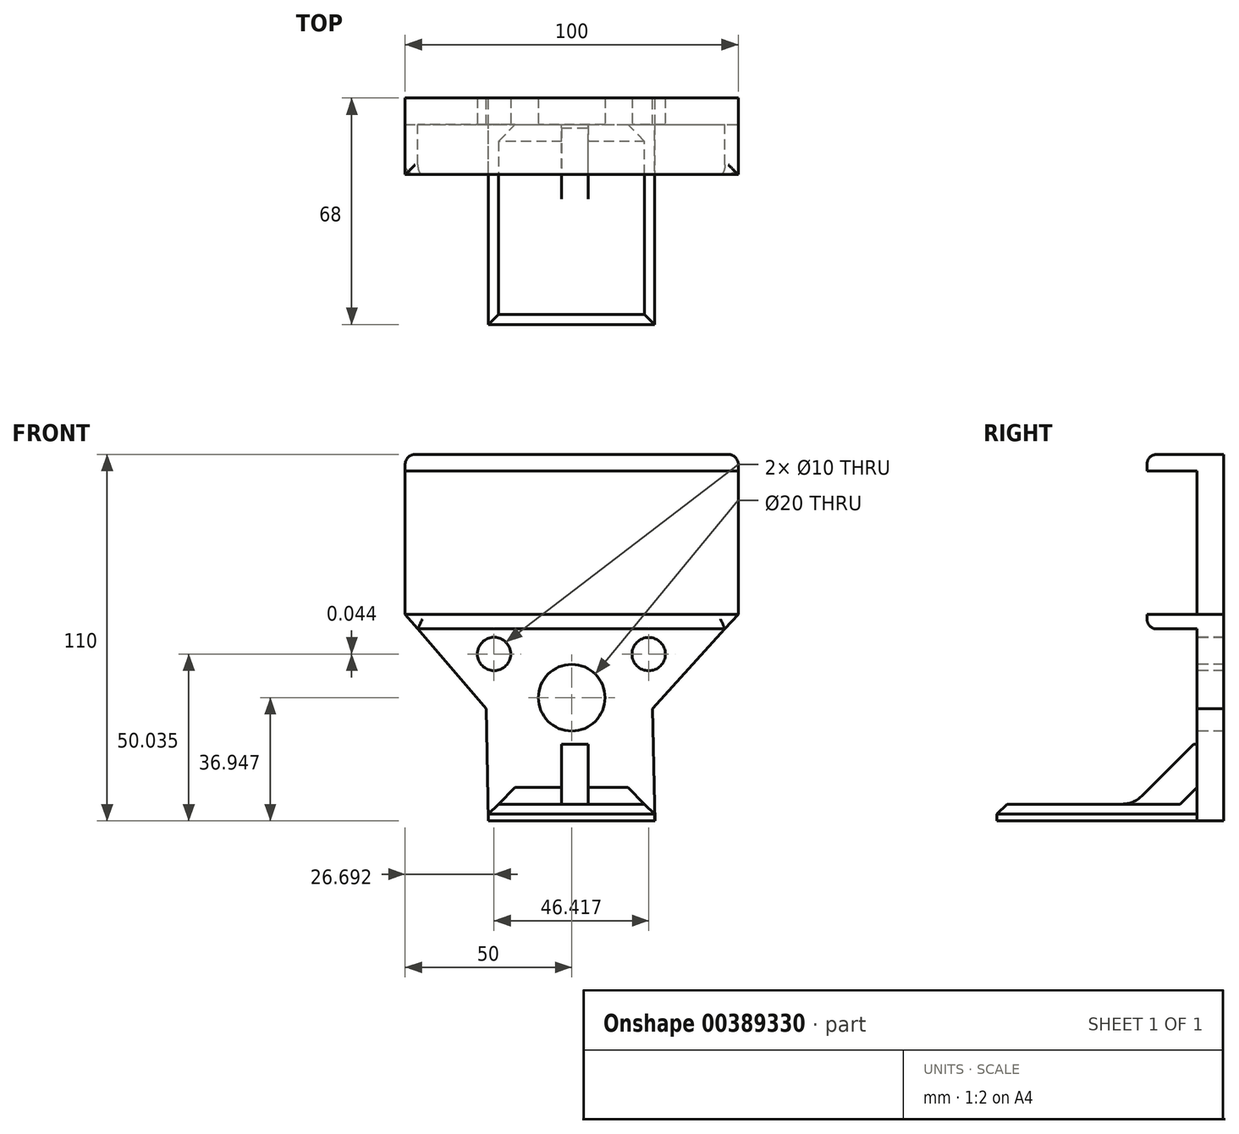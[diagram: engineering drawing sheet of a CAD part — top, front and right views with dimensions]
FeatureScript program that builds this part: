
annotation { "Feature Type Name" : "Feature", "Feature Type Description" : "" }
export const myFeature = defineFeature(function(context is Context, id is Id, definition is map)
    precondition{}
    {
        {
            var Q0;
            Q0=qCreatedBy(makeId("Front.planeOp"),FACE);
            var sketch = newSketch(context, id + "F0", { "sketchPlane" : qUnion([Q0])});
            skLineSegment(sketch, "E0", {"start": v(-25.7, 33.67) * mm, "end": v(-25, 0) * mm});
            skLineSegment(sketch, "E1", {"start": v(-25, 0) * mm, "end": v(0, 0) * mm});
            skLineSegment(sketch, "E2", {"start": v(24.3, 33.67) * mm, "end": v(25, 0) * mm});
            skLineSegment(sketch, "E3", {"start": v(25, 0) * mm, "end": v(0, 0) * mm});
            skLineSegment(sketch, "E4", {"start": v(-25.7, 33.67) * mm, "end": v(-50, 62) * mm});
            skLineSegment(sketch, "E5", {"start": v(24.3, 33.67) * mm, "end": v(50, 62) * mm});
            skLineSegment(sketch, "E6", {"start": v(-50, 62) * mm, "end": v(50, 62) * mm});
            skLineSegment(sketch, "E7", {"start": v(0, 62) * mm, "end": v(0, 0) * mm});
            skSolve(sketch);
        }
        {
            var Q0;
            Q0 = qSketchRegion(id + "F0", true);
            extrude(context, id + "F1", {"entities" : qUnion([Q0]), "depth" : 8 * mm, "offsetDistance" : 25 * mm});
        }
        {
            var Q0;
            Q0=makeQuery(id+"F1.opExtrude","CAP_FACE",FACE,{"disambiguationData":[OSD([sQuery(id+"F0.wireOp",EDGE,"E0"),sQuery(id+"F0.wireOp",EDGE,"E1"),sQuery(id+"F0.wireOp",EDGE,"E2"),sQuery(id+"F0.wireOp",EDGE,"E3"),sQuery(id+"F0.wireOp",EDGE,"E4"),sQuery(id+"F0.wireOp",EDGE,"E5"),sQuery(id+"F0.wireOp",EDGE,"E6")])],"isStart":false});
            var sketch = newSketch(context, id + "F2", { "sketchPlane" : qUnion([Q0])});
            skLineSegment(sketch, "E8.bottom", {"start": v(-25, 0) * mm, "end": v(24.9, 0) * mm});
            skLineSegment(sketch, "E8.top", {"start": v(-25, 5) * mm, "end": v(24.9, 5) * mm});
            skLineSegment(sketch, "E8.left", {"start": v(-25, 0) * mm, "end": v(-25, 5) * mm});
            skLineSegment(sketch, "E8.right", {"start": v(24.9, 0) * mm, "end": v(24.9, 5) * mm});
            skSolve(sketch);
        }
        {
            var Q0;
            Q0=makeQuery(id+"F2.imprint","IMPRINT",FACE,{"disambiguationData":[TD([[makeQuery(id+"F2.imprint","IMPRINT",EDGE,{"derivedFrom":sQuery(id+"F2.wireOp",EDGE,"E8.bottom")}),1.0]])]});
            extrude(context, id + "F3", {"entities" : qUnion([Q0]), "operationType" : NewBodyOperationType.ADD, "depth" : 60 * mm, "offsetDistance" : 25 * mm});
        }
        {
            var Q0;
            {var subQ0=sQuery(id+"F0.wireOp",EDGE,"E2");var subQ1=sQuery(id+"F0.wireOp",EDGE,"E6");var subQ2=sQuery(id+"F0.wireOp",EDGE,"E5");var subQ3=sQuery(id+"F0.wireOp",EDGE,"E4");var subQ4=sQuery(id+"F0.wireOp",EDGE,"E0");var subQ5=sQuery(id+"F0.wireOp",EDGE,"E3");var subQ6=sQuery(id+"F0.wireOp",EDGE,"E1");var subQ7=makeQuery(id+"F1.opExtrude","CAP_FACE",FACE,{"disambiguationData":[OSD([subQ4,subQ6,subQ0,subQ5,subQ3,subQ2,subQ1])],"isStart":false});Q0=makeQuery(id+"F3.boolean.opBoolean","SPLIT",FACE,{"disambiguationData":[TD([makeQuery(id+"F1.opExtrude","SWEPT_FACE",FACE,{"disambiguationData":[OSD([subQ4])]}),subQ7,makeQuery(id+"F1.opExtrude","SWEPT_FACE",FACE,{"disambiguationData":[OSD([subQ6,subQ5])]}),makeQuery(id+"F1.opExtrude","SWEPT_FACE",FACE,{"disambiguationData":[OSD([subQ0])]}),makeQuery(id+"F1.opExtrude","SWEPT_FACE",FACE,{"disambiguationData":[OSD([subQ3])]}),makeQuery(id+"F1.opExtrude","SWEPT_FACE",FACE,{"disambiguationData":[OSD([subQ2])]}),makeQuery(id+"F1.opExtrude","SWEPT_FACE",FACE,{"disambiguationData":[OSD([subQ1])]}),makeQuery(id+"F3.opExtrude","SWEPT_FACE",FACE,{"disambiguationData":[OSD([sQuery(id+"F2.wireOp",EDGE,"E8.bottom")])]}),makeQuery(id+"F3.opExtrude","SWEPT_FACE",FACE,{"disambiguationData":[OSD([sQuery(id+"F2.wireOp",EDGE,"E8.top")])]}),makeQuery(id+"F3.opExtrude","SWEPT_FACE",FACE,{"disambiguationData":[OSD([sQuery(id+"F2.wireOp",EDGE,"E8.left")])]}),makeQuery(id+"F3.opExtrude","SWEPT_FACE",FACE,{"disambiguationData":[OSD([sQuery(id+"F2.wireOp",EDGE,"E8.right")])]})])],"derivedFrom":subQ7});}
            var sketch = newSketch(context, id + "F4", { "sketchPlane" : qUnion([Q0])});
            skLineSegment(sketch, "E9.bottom", {"start": v(-3.01, 5) * mm, "end": v(4.99, 5) * mm});
            skLineSegment(sketch, "E9.top", {"start": v(-3.01, 23) * mm, "end": v(4.99, 23) * mm});
            skLineSegment(sketch, "E9.left", {"start": v(-3.01, 5) * mm, "end": v(-3.01, 23) * mm});
            skLineSegment(sketch, "E9.right", {"start": v(4.99, 5) * mm, "end": v(4.99, 23) * mm});
            skSolve(sketch);
        }
        {
            var Q0;
            Q0 = qSketchRegion(id + "F4", true);
            extrude(context, id + "F5", {"entities" : qUnion([Q0]), "operationType" : NewBodyOperationType.ADD, "depth" : 20 * mm, "offsetDistance" : 25 * mm});
        }
        {
            var Q0;
            Q0=makeQuery(id+"F5.opExtrude","CAP_EDGE",EDGE,{"disambiguationData":[OSD([sQuery(id+"F4.wireOp",EDGE,"E9.top")])],"isStart":false});
            chamfer(context, id + "F6", {"entities" : qUnion([Q0]), "width" : 19 * mm, "tangentPropagation" : true});
        }
        {
            var Q0;
            Q0=makeQuery(id+"F3.opExtrude","SWEPT_EDGE",EDGE,{"disambiguationData":[OSD([sQuery(id+"F2.wireOp",EDGE,"E8.top"),sQuery(id+"F2.wireOp",EDGE,"E8.left")])]});
            var Q1;
            Q1=makeQuery(id+"F3.opExtrude","CAP_EDGE",EDGE,{"disambiguationData":[OSD([sQuery(id+"F2.wireOp",EDGE,"E8.top")])],"isStart":false});
            var Q2;
            Q2=makeQuery(id+"F3.opExtrude","SWEPT_EDGE",EDGE,{"disambiguationData":[OSD([sQuery(id+"F0.wireOp",EDGE,"E2"),sQuery(id+"F2.wireOp",EDGE,"E8.top"),sQuery(id+"F2.wireOp",EDGE,"E8.right")])]});
            chamfer(context, id + "F7", {"entities" : qUnion([Q0, Q1, Q2]), "width" : 3 * mm, "tangentPropagation" : true});
        }
        {
            var Q0;
            {var subQ0=makeQuery(id+"F3.opExtrude","SWEPT_FACE",FACE,{"disambiguationData":[OSD([sQuery(id+"F2.wireOp",EDGE,"E8.bottom")])]});var subQ1=sQuery(id+"F0.wireOp",EDGE,"E2");var subQ2=makeQuery(id+"F1.opExtrude","SWEPT_FACE",FACE,{"disambiguationData":[OSD([subQ1])]});var subQ3=sQuery(id+"F0.wireOp",EDGE,"E6");var subQ4=makeQuery(id+"F3.opExtrude","SWEPT_FACE",FACE,{"disambiguationData":[OSD([sQuery(id+"F2.wireOp",EDGE,"E8.top")])]});var subQ5=sQuery(id+"F0.wireOp",EDGE,"E5");var subQ6=sQuery(id+"F0.wireOp",EDGE,"E4");var subQ7=sQuery(id+"F0.wireOp",EDGE,"E0");var subQ8=sQuery(id+"F0.wireOp",EDGE,"E3");var subQ9=sQuery(id+"F0.wireOp",EDGE,"E1");var subQ10=makeQuery(id+"F1.opExtrude","CAP_FACE",FACE,{"disambiguationData":[OSD([subQ7,subQ9,subQ1,subQ8,subQ6,subQ5,subQ3])],"isStart":false});var subQ11=makeQuery(id+"F1.opExtrude","SWEPT_FACE",FACE,{"disambiguationData":[OSD([subQ9,subQ8])]});var subQ12=makeQuery(id+"F3.opExtrude","SWEPT_FACE",FACE,{"disambiguationData":[OSD([sQuery(id+"F2.wireOp",EDGE,"E8.right")])]});Q0=makeQuery(id+"F7.opChamfer","MERGE",FACE,{"derivedFrom":[makeQuery(id+"F3.boolean.opBoolean","SPLIT",FACE,{"disambiguationData":[TD([subQ10,subQ11,subQ2,subQ0,subQ4,subQ12])],"derivedFrom":subQ10}),makeQuery(id+"F3.boolean.opBoolean","SPLIT",FACE,{"disambiguationData":[TD([makeQuery(id+"F1.opExtrude","SWEPT_FACE",FACE,{"disambiguationData":[OSD([subQ7])]}),subQ10,subQ11,subQ2,makeQuery(id+"F1.opExtrude","SWEPT_FACE",FACE,{"disambiguationData":[OSD([subQ6])]}),makeQuery(id+"F1.opExtrude","SWEPT_FACE",FACE,{"disambiguationData":[OSD([subQ5])]}),makeQuery(id+"F1.opExtrude","SWEPT_FACE",FACE,{"disambiguationData":[OSD([subQ3])]}),subQ0,subQ4,makeQuery(id+"F3.opExtrude","SWEPT_FACE",FACE,{"disambiguationData":[OSD([sQuery(id+"F2.wireOp",EDGE,"E8.left")])]}),subQ12])],"derivedFrom":subQ10})]});}
            var sketch = newSketch(context, id + "F8", { "sketchPlane" : qUnion([Q0])});
            skCircle(sketch, "E10", {"center": v(0, 36.95) * mm, "radius": 10 * mm});
            skCircle(sketch, "E11", {"center": v(-23.3, 50.08) * mm, "radius": 5 * mm});
            skCircle(sketch, "E12", {"center": v(23.1, 50.03) * mm, "radius": 5 * mm});
            skSolve(sketch);
        }
        {
            var Q0;
            Q0=makeQuery(id+"F8.imprint","IMPRINT",FACE,{"disambiguationData":[TD([[makeQuery(id+"F8.imprint","IMPRINT",EDGE,{"derivedFrom":sQuery(id+"F8.wireOp",EDGE,"E11")}),1.0]])]});
            var Q1;
            Q1=makeQuery(id+"F8.imprint","IMPRINT",FACE,{"disambiguationData":[TD([[makeQuery(id+"F8.imprint","IMPRINT",EDGE,{"derivedFrom":sQuery(id+"F8.wireOp",EDGE,"E10")}),1.0]])]});
            var Q2;
            Q2=makeQuery(id+"F8.imprint","IMPRINT",FACE,{"disambiguationData":[TD([[makeQuery(id+"F8.imprint","IMPRINT",EDGE,{"derivedFrom":sQuery(id+"F8.wireOp",EDGE,"E12")}),1.0]])]});
            var Q3;
            Q3=sQuery(id+"F8.wireOp",EDGE,"E11");
            var Q4;
            Q4=sQuery(id+"F8.wireOp",EDGE,"E10");
            var Q5;
            Q5=sQuery(id+"F8.wireOp",EDGE,"E12");
            extrude(context, id + "F9", {"entities" : qUnion([Q0, Q1, Q2]), "operationType" : NewBodyOperationType.REMOVE, "surfaceEntities" : qUnion([Q3, Q4, Q5]), "oppositeDirection" : true, "depth" : 25 * mm, "offsetDistance" : 25 * mm});
        }
        {
            var Q0;
            {var subQ0=sQuery(id+"F0.wireOp",EDGE,"E2");var subQ1=sQuery(id+"F0.wireOp",EDGE,"E6");var subQ2=sQuery(id+"F0.wireOp",EDGE,"E5");var subQ3=sQuery(id+"F0.wireOp",EDGE,"E4");var subQ4=sQuery(id+"F0.wireOp",EDGE,"E0");var subQ5=sQuery(id+"F0.wireOp",EDGE,"E3");var subQ6=sQuery(id+"F0.wireOp",EDGE,"E1");var subQ7=makeQuery(id+"F1.opExtrude","CAP_FACE",FACE,{"disambiguationData":[OSD([subQ4,subQ6,subQ0,subQ5,subQ3,subQ2,subQ1])],"isStart":false});Q0=makeQuery(id+"F6.opChamfer","BLEND_EDGE",EDGE,{"blendedFrom":[makeQuery(id+"F5.opExtrude","CAP_EDGE",EDGE,{"disambiguationData":[OSD([sQuery(id+"F4.wireOp",EDGE,"E9.top")])],"isStart":false}),makeQuery(id+"F3.boolean.opBoolean","SPLIT",FACE,{"disambiguationData":[TD([makeQuery(id+"F1.opExtrude","SWEPT_FACE",FACE,{"disambiguationData":[OSD([subQ4])]}),subQ7,makeQuery(id+"F1.opExtrude","SWEPT_FACE",FACE,{"disambiguationData":[OSD([subQ6,subQ5])]}),makeQuery(id+"F1.opExtrude","SWEPT_FACE",FACE,{"disambiguationData":[OSD([subQ0])]}),makeQuery(id+"F1.opExtrude","SWEPT_FACE",FACE,{"disambiguationData":[OSD([subQ3])]}),makeQuery(id+"F1.opExtrude","SWEPT_FACE",FACE,{"disambiguationData":[OSD([subQ2])]}),makeQuery(id+"F1.opExtrude","SWEPT_FACE",FACE,{"disambiguationData":[OSD([subQ1])]}),makeQuery(id+"F3.opExtrude","SWEPT_FACE",FACE,{"disambiguationData":[OSD([sQuery(id+"F2.wireOp",EDGE,"E8.bottom")])]}),makeQuery(id+"F3.opExtrude","SWEPT_FACE",FACE,{"disambiguationData":[OSD([sQuery(id+"F2.wireOp",EDGE,"E8.top")])]}),makeQuery(id+"F3.opExtrude","SWEPT_FACE",FACE,{"disambiguationData":[OSD([sQuery(id+"F2.wireOp",EDGE,"E8.left")])]}),makeQuery(id+"F3.opExtrude","SWEPT_FACE",FACE,{"disambiguationData":[OSD([sQuery(id+"F2.wireOp",EDGE,"E8.right")])]})])],"derivedFrom":subQ7})],"blendedInto":[makeQuery(id+"F3.boolean.opBoolean","SPLIT",FACE,{"disambiguationData":[TD([makeQuery(id+"F1.opExtrude","SWEPT_FACE",FACE,{"disambiguationData":[OSD([subQ4])]}),subQ7,makeQuery(id+"F1.opExtrude","SWEPT_FACE",FACE,{"disambiguationData":[OSD([subQ6,subQ5])]}),makeQuery(id+"F1.opExtrude","SWEPT_FACE",FACE,{"disambiguationData":[OSD([subQ0])]}),makeQuery(id+"F1.opExtrude","SWEPT_FACE",FACE,{"disambiguationData":[OSD([subQ3])]}),makeQuery(id+"F1.opExtrude","SWEPT_FACE",FACE,{"disambiguationData":[OSD([subQ2])]}),makeQuery(id+"F1.opExtrude","SWEPT_FACE",FACE,{"disambiguationData":[OSD([subQ1])]}),makeQuery(id+"F3.opExtrude","SWEPT_FACE",FACE,{"disambiguationData":[OSD([sQuery(id+"F2.wireOp",EDGE,"E8.bottom")])]}),makeQuery(id+"F3.opExtrude","SWEPT_FACE",FACE,{"disambiguationData":[OSD([sQuery(id+"F2.wireOp",EDGE,"E8.top")])]}),makeQuery(id+"F3.opExtrude","SWEPT_FACE",FACE,{"disambiguationData":[OSD([sQuery(id+"F2.wireOp",EDGE,"E8.left")])]}),makeQuery(id+"F3.opExtrude","SWEPT_FACE",FACE,{"disambiguationData":[OSD([sQuery(id+"F2.wireOp",EDGE,"E8.right")])]})])],"derivedFrom":subQ7})]});}
            var Q1;
            Q1=makeQuery(id+"F6.opChamfer","BLEND_EDGE",EDGE,{"blendedFrom":[makeQuery(id+"F5.opExtrude","CAP_EDGE",EDGE,{"disambiguationData":[OSD([sQuery(id+"F4.wireOp",EDGE,"E9.top")])],"isStart":false}),makeQuery(id+"F3.opExtrude","SWEPT_FACE",FACE,{"disambiguationData":[OSD([sQuery(id+"F2.wireOp",EDGE,"E8.top")])]})],"blendedInto":[makeQuery(id+"F3.opExtrude","SWEPT_FACE",FACE,{"disambiguationData":[OSD([sQuery(id+"F2.wireOp",EDGE,"E8.top")])]})]});
            var Q2;
            Q2=makeQuery(id+"F5.opExtrude","CAP_EDGE",EDGE,{"disambiguationData":[OSD([sQuery(id+"F4.wireOp",EDGE,"E9.top")])],"isStart":true});
            fillet(context, id + "F10", {"entities" : qUnion([Q0, Q1, Q2]), "radius" : 8 * mm, "tangentPropagation" : true, "allowEdgeOverflow" : false});
        }
        {
            var Q0;
            {var subQ0=sQuery(id+"F2.wireOp",EDGE,"E8.top");Q0=makeQuery(id+"F5.boolean.opBoolean","SPLIT",EDGE,{"disambiguationData":[TD([makeQuery(id+"F3.opExtrude","SWEPT_FACE",FACE,{"disambiguationData":[OSD([sQuery(id+"F2.wireOp",EDGE,"E8.left")])]})])],"derivedFrom":makeQuery(id+"F3.opExtrude","CAP_EDGE",EDGE,{"disambiguationData":[OSD([subQ0])],"isStart":true})});}
            var Q1;
            {var subQ0=sQuery(id+"F2.wireOp",EDGE,"E8.top");var subQ1=sQuery(id+"F0.wireOp",EDGE,"E2");Q1=makeQuery(id+"F5.boolean.opBoolean","SPLIT",EDGE,{"disambiguationData":[TD([makeQuery(id+"F1.opExtrude","SWEPT_FACE",FACE,{"disambiguationData":[OSD([subQ1])]})])],"derivedFrom":makeQuery(id+"F3.opExtrude","CAP_EDGE",EDGE,{"disambiguationData":[OSD([subQ0])],"isStart":true})});}
            chamfer(context, id + "F11", {"entities" : qUnion([Q0, Q1]), "width" : 5 * mm, "tangentPropagation" : true});
        }
        {
            var Q0;
            Q0=makeQuery(id+"F1.opExtrude","SWEPT_FACE",FACE,{"disambiguationData":[OSD([sQuery(id+"F0.wireOp",EDGE,"E6")])]});
            extrude(context, id + "F12", {"entities" : qUnion([Q0]), "operationType" : NewBodyOperationType.ADD, "depth" : 48 * mm, "offsetDistance" : 25 * mm});
        }
        {
            var Q0;
            {var subQ0=sQuery(id+"F0.wireOp",EDGE,"E6");var subQ1=makeQuery(id+"F3.opExtrude","SWEPT_FACE",FACE,{"disambiguationData":[OSD([sQuery(id+"F2.wireOp",EDGE,"E8.bottom")])]});var subQ2=sQuery(id+"F0.wireOp",EDGE,"E2");var subQ3=makeQuery(id+"F1.opExtrude","SWEPT_FACE",FACE,{"disambiguationData":[OSD([subQ2])]});var subQ4=makeQuery(id+"F3.opExtrude","SWEPT_FACE",FACE,{"disambiguationData":[OSD([sQuery(id+"F2.wireOp",EDGE,"E8.top")])]});var subQ5=sQuery(id+"F0.wireOp",EDGE,"E5");var subQ6=sQuery(id+"F0.wireOp",EDGE,"E4");var subQ7=sQuery(id+"F0.wireOp",EDGE,"E0");var subQ8=sQuery(id+"F0.wireOp",EDGE,"E3");var subQ9=sQuery(id+"F0.wireOp",EDGE,"E1");var subQ10=makeQuery(id+"F1.opExtrude","CAP_FACE",FACE,{"disambiguationData":[OSD([subQ7,subQ9,subQ2,subQ8,subQ6,subQ5,subQ0])],"isStart":false});var subQ11=makeQuery(id+"F1.opExtrude","SWEPT_FACE",FACE,{"disambiguationData":[OSD([subQ9,subQ8])]});var subQ12=makeQuery(id+"F3.opExtrude","SWEPT_FACE",FACE,{"disambiguationData":[OSD([sQuery(id+"F2.wireOp",EDGE,"E8.right")])]});Q0=makeQuery(id+"F12.boolean.opBoolean","MERGE",FACE,{"derivedFrom":[makeQuery(id+"F7.opChamfer","MERGE",FACE,{"derivedFrom":[makeQuery(id+"F3.boolean.opBoolean","SPLIT",FACE,{"disambiguationData":[TD([subQ10,subQ11,subQ3,subQ1,subQ4,subQ12])],"derivedFrom":subQ10}),makeQuery(id+"F3.boolean.opBoolean","SPLIT",FACE,{"disambiguationData":[TD([makeQuery(id+"F1.opExtrude","SWEPT_FACE",FACE,{"disambiguationData":[OSD([subQ7])]}),subQ10,subQ11,subQ3,makeQuery(id+"F1.opExtrude","SWEPT_FACE",FACE,{"disambiguationData":[OSD([subQ6])]}),makeQuery(id+"F1.opExtrude","SWEPT_FACE",FACE,{"disambiguationData":[OSD([subQ5])]}),makeQuery(id+"F1.opExtrude","SWEPT_FACE",FACE,{"disambiguationData":[OSD([subQ0])]}),subQ1,subQ4,makeQuery(id+"F3.opExtrude","SWEPT_FACE",FACE,{"disambiguationData":[OSD([sQuery(id+"F2.wireOp",EDGE,"E8.left")])]}),subQ12])],"derivedFrom":subQ10})]}),makeQuery(id+"F12.opExtrude","SWEPT_FACE",FACE,{"disambiguationData":[OSD([subQ0]),TDD([makeQuery(id+"F1.opExtrude","CAP_EDGE",EDGE,{"disambiguationData":[OSD([subQ0])],"isStart":false})])]})]});}
            var sketch = newSketch(context, id + "F13", { "sketchPlane" : qUnion([Q0])});
            skLineSegment(sketch, "E13", {"start": v(-50, 62) * mm, "end": v(50, 62) * mm});
            skLineSegment(sketch, "E14", {"start": v(-50, 62) * mm, "end": v(-46.21, 57.59) * mm});
            skLineSegment(sketch, "E15", {"start": v(-46.21, 57.59) * mm, "end": v(46, 57.59) * mm});
            skLineSegment(sketch, "E16", {"start": v(46, 57.59) * mm, "end": v(50, 62) * mm});
            skSolve(sketch);
        }
        {
            var Q0;
            Q0=makeQuery(id+"F13.imprint","IMPRINT",FACE,{"disambiguationData":[TD([[makeQuery(id+"F13.imprint","IMPRINT",EDGE,{"derivedFrom":sQuery(id+"F13.wireOp",EDGE,"E13")}),-1.0]])]});
            extrude(context, id + "F14", {"entities" : qUnion([Q0]), "operationType" : NewBodyOperationType.ADD, "depth" : 15 * mm, "offsetDistance" : 25 * mm});
        }
        {
            var Q0;
            {var subQ0=sQuery(id+"F0.wireOp",EDGE,"E6");var subQ1=sQuery(id+"F0.wireOp",EDGE,"E4");var subQ2=sQuery(id+"F0.wireOp",EDGE,"E5");var subQ3=makeQuery(id+"F1.opExtrude","SWEPT_FACE",FACE,{"disambiguationData":[OSD([subQ2])]});var subQ4=makeQuery(id+"F1.opExtrude","SWEPT_FACE",FACE,{"disambiguationData":[OSD([subQ1])]});var subQ5=makeQuery(id+"F3.opExtrude","SWEPT_FACE",FACE,{"disambiguationData":[OSD([sQuery(id+"F2.wireOp",EDGE,"E8.bottom")])]});var subQ6=sQuery(id+"F0.wireOp",EDGE,"E2");var subQ7=makeQuery(id+"F1.opExtrude","SWEPT_FACE",FACE,{"disambiguationData":[OSD([subQ6])]});var subQ8=makeQuery(id+"F3.opExtrude","SWEPT_FACE",FACE,{"disambiguationData":[OSD([sQuery(id+"F2.wireOp",EDGE,"E8.top")])]});var subQ9=sQuery(id+"F0.wireOp",EDGE,"E0");var subQ10=sQuery(id+"F0.wireOp",EDGE,"E3");var subQ11=sQuery(id+"F0.wireOp",EDGE,"E1");var subQ12=makeQuery(id+"F1.opExtrude","CAP_FACE",FACE,{"disambiguationData":[OSD([subQ9,subQ11,subQ6,subQ10,subQ1,subQ2,subQ0])],"isStart":false});var subQ13=makeQuery(id+"F1.opExtrude","SWEPT_FACE",FACE,{"disambiguationData":[OSD([subQ11,subQ10])]});var subQ14=makeQuery(id+"F3.opExtrude","SWEPT_FACE",FACE,{"disambiguationData":[OSD([sQuery(id+"F2.wireOp",EDGE,"E8.right")])]});Q0=makeQuery(id+"F14.boolean.opBoolean","SPLIT",FACE,{"disambiguationData":[TD([makeQuery(id+"F12.opExtrude","CAP_FACE",FACE,{"disambiguationData":[OSD([subQ0])],"isStart":false})])],"derivedFrom":makeQuery(id+"F12.boolean.opBoolean","MERGE",FACE,{"derivedFrom":[makeQuery(id+"F7.opChamfer","MERGE",FACE,{"derivedFrom":[makeQuery(id+"F3.boolean.opBoolean","SPLIT",FACE,{"disambiguationData":[TD([subQ12,subQ13,subQ7,subQ5,subQ8,subQ14])],"derivedFrom":subQ12}),makeQuery(id+"F3.boolean.opBoolean","SPLIT",FACE,{"disambiguationData":[TD([makeQuery(id+"F1.opExtrude","SWEPT_FACE",FACE,{"disambiguationData":[OSD([subQ9])]}),subQ12,subQ13,subQ7,subQ4,subQ3,makeQuery(id+"F1.opExtrude","SWEPT_FACE",FACE,{"disambiguationData":[OSD([subQ0])]}),subQ5,subQ8,makeQuery(id+"F3.opExtrude","SWEPT_FACE",FACE,{"disambiguationData":[OSD([sQuery(id+"F2.wireOp",EDGE,"E8.left")])]}),subQ14])],"derivedFrom":subQ12})]}),makeQuery(id+"F12.opExtrude","SWEPT_FACE",FACE,{"disambiguationData":[OSD([subQ0]),TDD([makeQuery(id+"F1.opExtrude","CAP_EDGE",EDGE,{"disambiguationData":[OSD([subQ0])],"isStart":false})])]})]})});}
            var sketch = newSketch(context, id + "F15", { "sketchPlane" : qUnion([Q0])});
            skLineSegment(sketch, "E17.bottom", {"start": v(-50, 110) * mm, "end": v(50, 110) * mm});
            skLineSegment(sketch, "E17.top", {"start": v(-50, 105) * mm, "end": v(50, 105) * mm});
            skLineSegment(sketch, "E17.left", {"start": v(-50, 110) * mm, "end": v(-50, 105) * mm});
            skLineSegment(sketch, "E17.right", {"start": v(50, 110) * mm, "end": v(50, 105) * mm});
            skSolve(sketch);
        }
        {
            var Q0;
            Q0 = qSketchRegion(id + "F15", true);
            extrude(context, id + "F16", {"entities" : qUnion([Q0]), "operationType" : NewBodyOperationType.ADD, "depth" : 15 * mm, "offsetDistance" : 25 * mm});
        }
        {
            var Q0;
            Q0=makeQuery(id+"F16.boolean.opBoolean","MERGE",EDGE,{"derivedFrom":[makeQuery(id+"F12.opExtrude","CAP_EDGE",EDGE,{"disambiguationData":[OSD([sQuery(id+"F0.wireOp",EDGE,"E5"),sQuery(id+"F0.wireOp",EDGE,"E6")])],"isStart":false}),makeQuery(id+"F16.opExtrude","SWEPT_EDGE",EDGE,{"disambiguationData":[OSD([sQuery(id+"F15.wireOp",EDGE,"E17.bottom"),sQuery(id+"F15.wireOp",EDGE,"E17.right")])]})]});
            var Q1;
            Q1=makeQuery(id+"F16.boolean.opBoolean","MERGE",EDGE,{"derivedFrom":[makeQuery(id+"F12.opExtrude","CAP_EDGE",EDGE,{"disambiguationData":[OSD([sQuery(id+"F0.wireOp",EDGE,"E4"),sQuery(id+"F0.wireOp",EDGE,"E6")])],"isStart":false}),makeQuery(id+"F16.opExtrude","SWEPT_EDGE",EDGE,{"disambiguationData":[OSD([sQuery(id+"F15.wireOp",EDGE,"E17.bottom"),sQuery(id+"F15.wireOp",EDGE,"E17.left")])]})]});
            var Q2;
            Q2=makeQuery(id+"F16.opExtrude","CAP_EDGE",EDGE,{"disambiguationData":[OSD([sQuery(id+"F15.wireOp",EDGE,"E17.bottom")])],"isStart":false});
            var Q3;
            Q3=makeQuery(id+"F14.opExtrude","CAP_EDGE",EDGE,{"disambiguationData":[OSD([sQuery(id+"F13.wireOp",EDGE,"E15")])],"isStart":false});
            var Q4;
            Q4=makeQuery(id+"F14.opExtrude","CAP_EDGE",EDGE,{"disambiguationData":[OSD([sQuery(id+"F13.wireOp",EDGE,"E16")])],"isStart":false});
            var Q5;
            Q5=makeQuery(id+"F14.opExtrude","CAP_EDGE",EDGE,{"disambiguationData":[OSD([sQuery(id+"F13.wireOp",EDGE,"E14")])],"isStart":false});
            fillet(context, id + "F17", {"entities" : qUnion([Q0, Q1, Q2, Q3, Q4, Q5]), "radius" : 3 * mm, "tangentPropagation" : true, "allowEdgeOverflow" : false});
        }
    });
